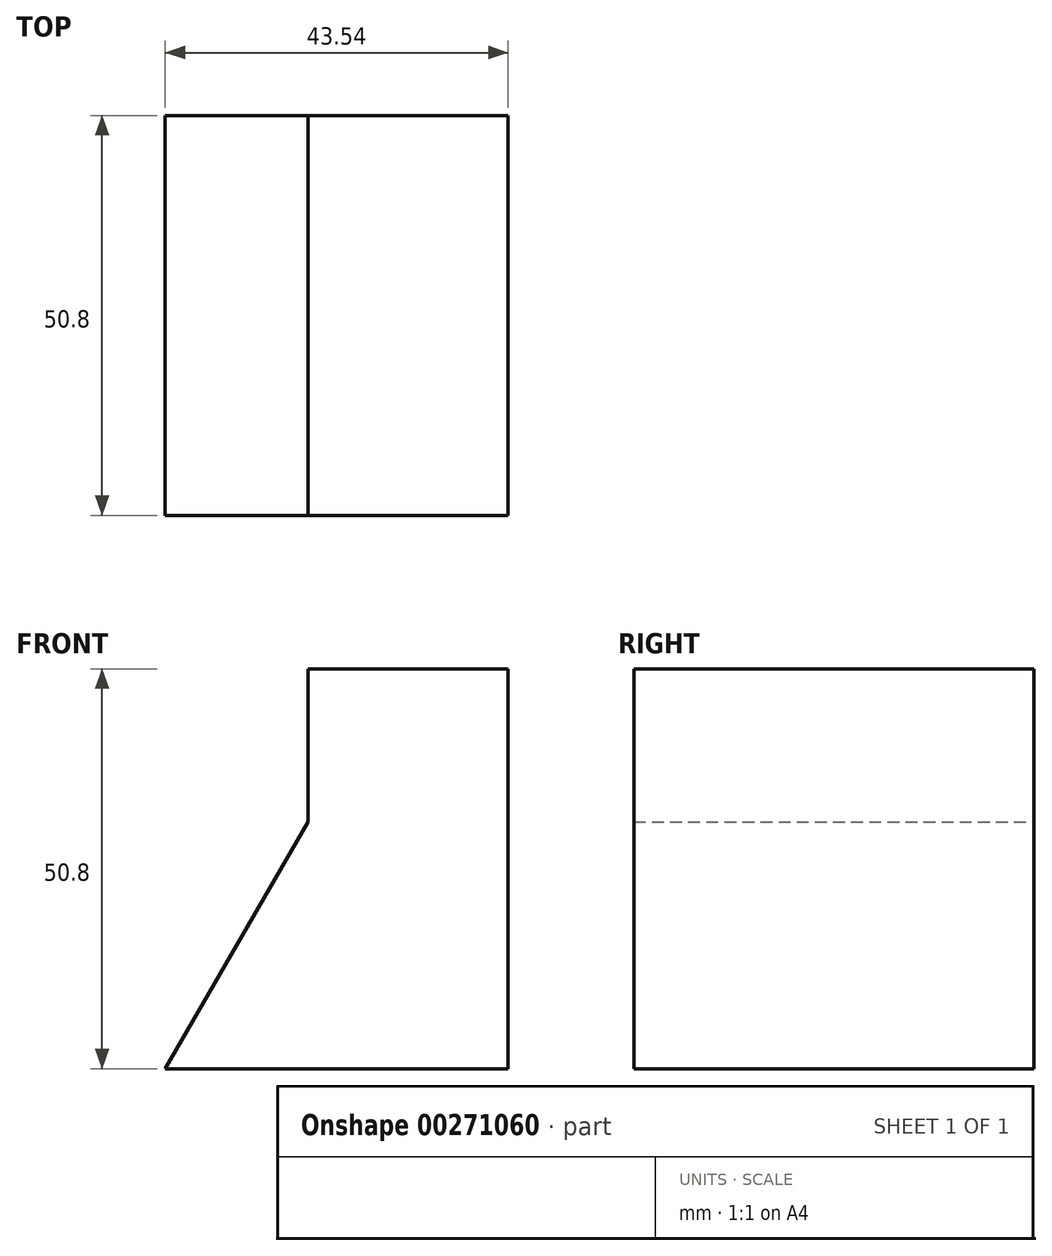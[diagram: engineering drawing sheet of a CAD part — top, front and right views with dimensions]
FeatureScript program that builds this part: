
annotation { "Feature Type Name" : "Feature", "Feature Type Description" : "" }
export const myFeature = defineFeature(function(context is Context, id is Id, definition is map)
    precondition{}
    {
        {
            var Q0;
            Q0=qCreatedBy(makeId("Front.planeOp"),FACE);
            var sketch = newSketch(context, id + "F0", { "sketchPlane" : qUnion([Q0])});
            skLineSegment(sketch, "E0", {"start": v(0, 0) * mm, "end": v(0, 50.8) * mm});
            skLineSegment(sketch, "E1", {"start": v(0, 50.8) * mm, "end": v(-25.4, 50.8) * mm});
            skLineSegment(sketch, "E2", {"start": v(-25.4, 50.8) * mm, "end": v(-25.4, 31.32) * mm});
            skLineSegment(sketch, "E3", {"start": v(-25.4, 31.32) * mm, "end": v(-43.54, 0) * mm});
            skLineSegment(sketch, "E4", {"start": v(-43.54, 0) * mm, "end": v(0, 0) * mm});
            skSolve(sketch);
        }
        {
            var Q0;
            Q0 = qSketchRegion(id + "F0", true);
            extrude(context, id + "F1", {"entities" : qUnion([Q0]), "depth" : 50.8 * mm});
        }
    });
